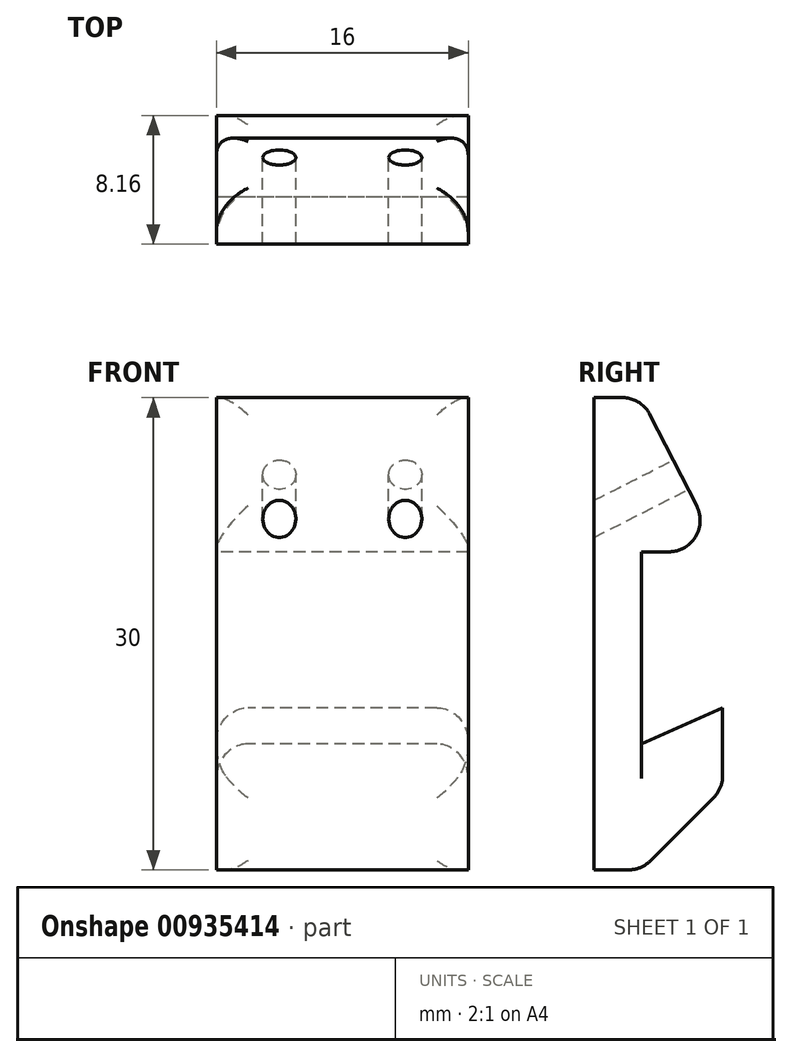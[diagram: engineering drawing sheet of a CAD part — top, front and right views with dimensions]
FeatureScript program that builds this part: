
annotation { "Feature Type Name" : "Feature", "Feature Type Description" : "" }
export const myFeature = defineFeature(function(context is Context, id is Id, definition is map)
    precondition{}
    {
        {
            var Q0;
            Q0=qCreatedBy(makeId("Right.planeOp"),FACE);
            var sketch = newSketch(context, id + "F0", { "sketchPlane" : qUnion([Q0])});
            skLineSegment(sketch, "E0.bottom", {"start": v(1.5, -15) * mm, "end": v(-1.5, -15) * mm});
            skLineSegment(sketch, "E0.top", {"start": v(1.5, 15) * mm, "end": v(-1.5, 15) * mm});
            skLineSegment(sketch, "E0.left", {"start": v(1.5, -15) * mm, "end": v(1.5, 15) * mm});
            skLineSegment(sketch, "E0.right", {"start": v(-1.5, -15) * mm, "end": v(-1.5, 15) * mm});
            skPoint(sketch, "E0.middle", {"position": v(0, 0) * mm});
            skLineSegment(sketch, "E1", {"start": v(1.5, 15) * mm, "end": v(6.5, 5.2) * mm});
            skLineSegment(sketch, "E2", {"start": v(6.5, 5.2) * mm, "end": v(1.5, 5.2) * mm});
            skLineSegment(sketch, "E3", {"start": v(1.5, 5.2) * mm, "end": v(1.5, -15) * mm});
            skLineSegment(sketch, "E4", {"start": v(1.5, -15) * mm, "end": v(13.5, -3) * mm});
            skLineSegment(sketch, "E5", {"start": v(13.5, -3) * mm, "end": v(10.5, -3) * mm});
            skLineSegment(sketch, "E6", {"start": v(10.5, -3) * mm, "end": v(1.5, -7) * mm});
            skLineSegment(sketch, "E7", {"start": v(10.5, -3) * mm, "end": v(1.5, -3) * mm});
            skLineSegment(sketch, "E8", {"start": v(6.66, -4.7) * mm, "end": v(6.66, -9.84) * mm});
            skArc(sketch, "E9", {"start": v(6.66, -4.7) * mm, "mid": v(5.57, -4.23) * mm, "end": v(5.19, -5.36) * mm});
            skSolve(sketch);
        }
        {
            var Q0;
            {var subQ1=sQuery(id+"F0.wireOp",EDGE,"E0.bottom");Q0=makeQuery(id+"F0.imprint","IMPRINT",FACE,{"disambiguationData":[TD([[makeQuery(id+"F0.imprint","IMPRINT",EDGE,{"derivedFrom":subQ1}),-1.0]])]});}
            var Q1;
            Q1=makeQuery(id+"F0.imprint","IMPRINT",FACE,{"disambiguationData":[TD([[makeQuery(id+"F0.imprint","IMPRINT",EDGE,{"derivedFrom":sQuery(id+"F0.wireOp",EDGE,"E0.left")}),-1.0]])]});
            var Q2;
            {var subQ5=sQuery(id+"F0.wireOp",EDGE,"E8");Q2=makeQuery(id+"F0.imprint","IMPRINT",FACE,{"disambiguationData":[TD([[makeQuery(id+"F0.imprint","IMPRINT",EDGE,{"derivedFrom":subQ5}),-1.0]])]});}
            extrude(context, id + "F1", {"entities" : qUnion([Q0, Q1, Q2]), "depth" : 16 * mm, "offsetDistance" : 25 * mm});
        }
        {
            var Q0;
            Q0=makeQuery(id+"F1.opExtrude","SWEPT_FACE",FACE,{"disambiguationData":[OSD([sQuery(id+"F0.wireOp",EDGE,"E1")])]});
            var sketch = newSketch(context, id + "F2", { "sketchPlane" : qUnion([Q0])});
            skLineSegment(sketch, "E10", {"start": v(-16, 7.18) * mm, "end": v(0, 7.18) * mm, "construction": true});
            skLineSegment(sketch, "E11", {"start": v(-8, 12.68) * mm, "end": v(-8, 1.68) * mm, "construction": true});
            skLineSegment(sketch, "E12", {"start": v(-16, 12.68) * mm, "end": v(-8, 1.68) * mm, "construction": true});
            skLineSegment(sketch, "E13", {"start": v(0, 12.68) * mm, "end": v(-8, 1.68) * mm, "construction": true});
            skCircle(sketch, "E14", {"center": v(-12, 7.18) * mm, "radius": 1.05 * mm});
            skCircle(sketch, "E15", {"center": v(-4, 7.18) * mm, "radius": 1.05 * mm});
            skSolve(sketch);
        }
        {
            var Q0;
            Q0=makeQuery(id+"F2.imprint","IMPRINT",FACE,{"disambiguationData":[TD([[makeQuery(id+"F2.imprint","IMPRINT",EDGE,{"derivedFrom":sQuery(id+"F2.wireOp",EDGE,"E14")}),1.0]])]});
            var Q1;
            Q1=makeQuery(id+"F2.imprint","IMPRINT",FACE,{"disambiguationData":[TD([[makeQuery(id+"F2.imprint","IMPRINT",EDGE,{"derivedFrom":sQuery(id+"F2.wireOp",EDGE,"E15")}),1.0]])]});
            var Q2;
            Q2=makeQuery(id+"F1.opExtrude","SWEPT_FACE",FACE,{"disambiguationData":[OSD([sQuery(id+"F0.wireOp",EDGE,"E0.right")])]});
            extrude(context, id + "F3", {"entities" : qUnion([Q0, Q1]), "operationType" : NewBodyOperationType.REMOVE, "endBound" : BoundingType.UP_TO_SURFACE, "oppositeDirection" : true, "depth" : 25 * mm, "endBoundEntityFace" : qUnion([Q2]), "offsetDistance" : 25 * mm});
        }
        {
            var Q0;
            Q0=makeQuery(id+"F1.opExtrude","CAP_EDGE",EDGE,{"disambiguationData":[OSD([sQuery(id+"F0.wireOp",EDGE,"E3")])],"isStart":false});
            var Q1;
            Q1=makeQuery(id+"F1.opExtrude","CAP_EDGE",EDGE,{"disambiguationData":[OSD([sQuery(id+"F0.wireOp",EDGE,"E3")])],"isStart":true});
            var Q2;
            Q2=makeQuery(id+"F1.opExtrude","CAP_EDGE",EDGE,{"disambiguationData":[OSD([sQuery(id+"F0.wireOp",EDGE,"E1")])],"isStart":false});
            var Q3;
            Q3=makeQuery(id+"F1.opExtrude","CAP_EDGE",EDGE,{"disambiguationData":[OSD([sQuery(id+"F0.wireOp",EDGE,"E1")])],"isStart":true});
            var Q4;
            Q4=makeQuery(id+"F1.opExtrude","SWEPT_EDGE",EDGE,{"disambiguationData":[OSD([sQuery(id+"F0.wireOp",EDGE,"E1"),sQuery(id+"F0.wireOp",EDGE,"E2")])]});
            var Q5;
            Q5=makeQuery(id+"F1.opExtrude","SWEPT_EDGE",EDGE,{"disambiguationData":[OSD([sQuery(id+"F0.wireOp",EDGE,"E4"),sQuery(id+"F0.wireOp",EDGE,"E5")])]});
            var Q6;
            Q6=makeQuery(id+"F1.opExtrude","CAP_EDGE",EDGE,{"disambiguationData":[OSD([sQuery(id+"F0.wireOp",EDGE,"E4")])],"isStart":false});
            var Q7;
            Q7=makeQuery(id+"F1.opExtrude","CAP_EDGE",EDGE,{"disambiguationData":[OSD([sQuery(id+"F0.wireOp",EDGE,"E4")])],"isStart":true});
            var Q8;
            Q8=makeQuery(id+"F1.opExtrude","CAP_EDGE",EDGE,{"disambiguationData":[OSD([sQuery(id+"F0.wireOp",EDGE,"E6")])],"isStart":false});
            var Q9;
            Q9=makeQuery(id+"F1.opExtrude","CAP_EDGE",EDGE,{"disambiguationData":[OSD([sQuery(id+"F0.wireOp",EDGE,"E6")])],"isStart":true});
            var Q10;
            Q10=makeQuery(id+"F1.opExtrude","SWEPT_EDGE",EDGE,{"disambiguationData":[OSD([sQuery(id+"F0.wireOp",EDGE,"E0.top"),sQuery(id+"F0.wireOp",EDGE,"E0.left"),sQuery(id+"F0.wireOp",EDGE,"E1")])]});
            var Q11;
            Q11=makeQuery(id+"F1.opExtrude","SWEPT_FACE",FACE,{"disambiguationData":[OSD([sQuery(id+"F0.wireOp",EDGE,"E4")])]});
            fillet(context, id + "F4", {"entities" : qUnion([Q0, Q1, Q2, Q3, Q4, Q5, Q6, Q7, Q8, Q9, Q10, Q11]), "radius" : 2 * mm, "tangentPropagation" : true, "allowEdgeOverflow" : false});
        }
    });
